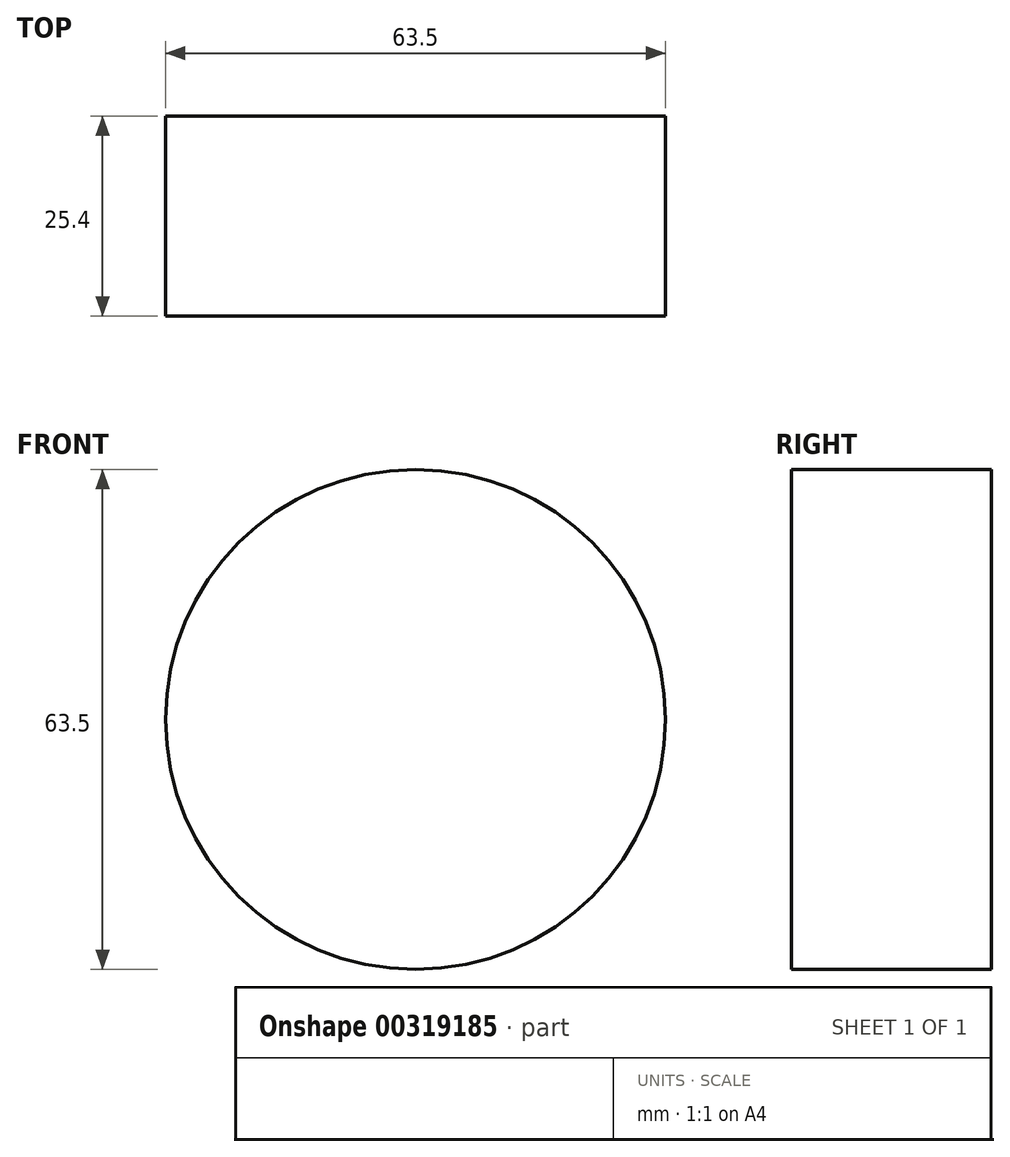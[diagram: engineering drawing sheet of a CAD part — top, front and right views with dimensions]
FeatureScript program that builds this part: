
annotation { "Feature Type Name" : "Feature", "Feature Type Description" : "" }
export const myFeature = defineFeature(function(context is Context, id is Id, definition is map)
    precondition{}
    {
        {
            var Q0;
            Q0=qCreatedBy(makeId("Front.planeOp"),FACE);
            var sketch = newSketch(context, id + "F0", { "sketchPlane" : qUnion([Q0])});
            skLineSegment(sketch, "E0.bottom", {"start": v(0, 0) * mm, "end": v(63.5, 0) * mm});
            skLineSegment(sketch, "E0.top", {"start": v(0, 63.5) * mm, "end": v(63.5, 63.5) * mm});
            skLineSegment(sketch, "E0.left", {"start": v(0, 0) * mm, "end": v(0, 63.5) * mm});
            skLineSegment(sketch, "E0.right", {"start": v(63.5, 0) * mm, "end": v(63.5, 63.5) * mm});
            skCircle(sketch, "E1", {"center": v(31.75, 31.75) * mm, "radius": 31.75 * mm});
            skPoint(sketch, "E1.first.point", {"position": v(0, 31.75) * mm});
            skPoint(sketch, "E1.second.point", {"position": v(63.5, 31.75) * mm});
            skPoint(sketch, "E1.third.point", {"position": v(31.75, 0) * mm});
            skSolve(sketch);
        }
        {
            var Q0;
            {var subQ0=sQuery(id+"F0.wireOp",EDGE,"E1");var subQ1=makeQuery(id+"F0.imprint","INTERSECT",VERTEX,{"derivedFrom":[sQuery(id+"F0.wireOp",EDGE,"E0.top"),subQ0]});Q0=makeQuery(id+"F0.imprint","IMPRINT",FACE,{"disambiguationData":[TD([[makeQuery(id+"F0.imprint","IMPRINT",EDGE,{"disambiguationData":[TD([[subQ1,1.0]])],"derivedFrom":subQ0}),1.0]])]});}
            extrude(context, id + "F1", {"entities" : qUnion([Q0]), "depth" : 25.4 * mm});
        }
    });
